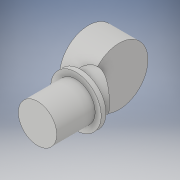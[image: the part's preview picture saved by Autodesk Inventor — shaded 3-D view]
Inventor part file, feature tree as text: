
AUTODESK INVENTOR PART (.ipt)
format: ipt  version: 2018.2 (Build 222227000, 227)  size: 133,632 bytes
history: native  units: in
note: dims shown in document units (in); Inventor stores cm internally (conversion verified against a paired STEP export)
features: extrude x4, other x4, sketch x4, plane x2
ambient origin geometry x8: Origin, YZ Plane, XZ Plane, XY Plane, X Axis, Y Axis, Z Axis, Center Point
bodies: Solid1 (feature_tree)
feature tree (14):
  extrude  "Extrusion1"  Depth=1.315in
  plane  "Work Plane1"
  extrude  "Extrusion2"  [1 undecoded]
  other  "Work Axis1"
  sketch  "Sketch4"  dims[d6=1.315in d7=0.125in d8=0.0in]
  other  "Work Point2"
  plane  "Work Plane2"
  sketch  "Sketch5"  dims[d9=1.5in d10=0.5in d11=0.0in d12=0.8in d13=0.0in]
  extrude  "Extrusion3"  Depth=0.125in TaperAngle=0.0deg
  extrude  "Extrusion4"  Depth=0.8in TaperAngle=0.0deg
  sketch  "Sketch1"  dims[d0=1.0in d1=1.315in]
  sketch  "Sketch3"  dims[d2=2.125in d3=0.0in d5=-1.0in]
  other  "Work Point1"
  other  "Work Point3"
note: 1 required parameter value undecoded (feature->parameter linkage not recoverable at this tier; creation-order binding heuristic only, values carry confidence <= 0.55)
